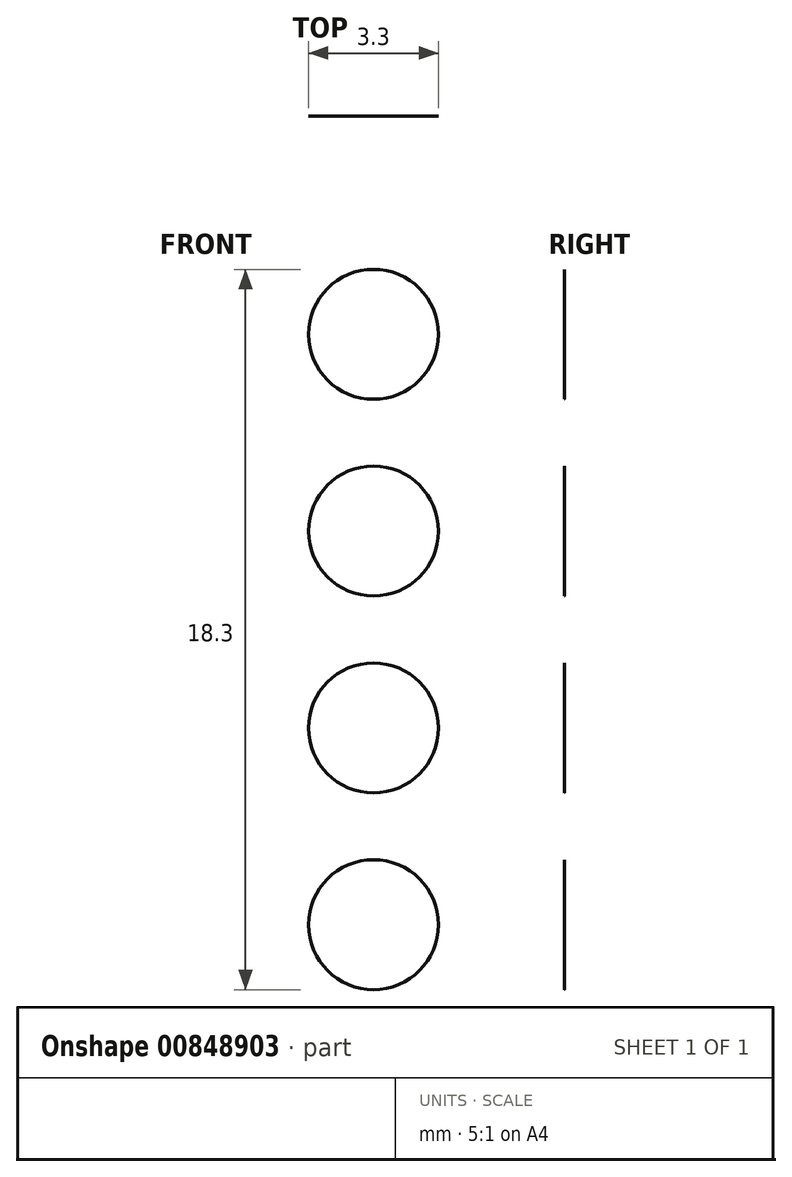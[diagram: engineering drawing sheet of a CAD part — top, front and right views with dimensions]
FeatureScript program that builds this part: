
annotation { "Feature Type Name" : "Feature", "Feature Type Description" : "" }
export const myFeature = defineFeature(function(context is Context, id is Id, definition is map)
    precondition{}
    {
        {
            var Q0;
            Q0=qCreatedBy(makeId("Front.planeOp"),FACE);
            var sketch = newSketch(context, id + "F0", { "sketchPlane" : qUnion([Q0])});
            skCircle(sketch, "E0", {"center": v(0, 0) * mm, "radius": 1.59 * mm});
            skLineSegment(sketch, "E1.direction1", {"start": v(0, 0) * mm, "end": v(25, 0) * mm, "construction": true});
            skLineSegment(sketch, "E2", {"start": v(0, 0) * mm, "end": v(0, 35.3) * mm, "construction": true});
            skCircle(sketch, "E3.0.1.0", {"center": v(0, 5) * mm, "radius": 1.59 * mm});
            skCircle(sketch, "E3.0.2.0", {"center": v(0, 10) * mm, "radius": 1.59 * mm});
            skCircle(sketch, "E3.0.3.0", {"center": v(0, 15) * mm, "radius": 1.59 * mm});
            skLineSegment(sketch, "E3.direction2", {"start": v(0, 0) * mm, "end": v(0, 5) * mm, "construction": true});
            skCircle(sketch, "E4", {"center": v(0, 20) * mm, "radius": 1.65 * mm});
            skLineSegment(sketch, "E5.direction2", {"start": v(0, 20) * mm, "end": v(0, 25) * mm, "construction": true});
            skCircle(sketch, "E6.0.1.0", {"center": v(0, 25) * mm, "radius": 1.65 * mm});
            skCircle(sketch, "E6.0.2.0", {"center": v(0, 30) * mm, "radius": 1.65 * mm});
            skCircle(sketch, "E6.0.3.0", {"center": v(0, 35) * mm, "radius": 1.65 * mm});
            skLineSegment(sketch, "E6.direction1", {"start": v(0, 20) * mm, "end": v(25, 20) * mm, "construction": true});
            skLineSegment(sketch, "E7", {"start": v(0, 0) * mm, "end": v(0, -5) * mm, "construction": true});
            skCircle(sketch, "E8", {"center": v(0, -5) * mm, "radius": 1.5 * mm});
            skCircle(sketch, "E9.0.1.0", {"center": v(0, -10) * mm, "radius": 1.5 * mm});
            skCircle(sketch, "E9.0.2.0", {"center": v(0, -15) * mm, "radius": 1.5 * mm});
            skCircle(sketch, "E9.0.3.0", {"center": v(0, -20) * mm, "radius": 1.5 * mm});
            skLineSegment(sketch, "E9.direction1", {"start": v(0, -5) * mm, "end": v(25, -5) * mm, "construction": true});
            skLineSegment(sketch, "E9.direction2", {"start": v(0, -5) * mm, "end": v(0, -10) * mm, "construction": true});
            skSolve(sketch);
        }
        {
            var Q0;
            Q0=makeQuery(id+"F0.imprint","IMPRINT",FACE,{"disambiguationData":[TD([[makeQuery(id+"F0.imprint","IMPRINT",EDGE,{"derivedFrom":sQuery(id+"F0.wireOp",EDGE,"E6.0.3.0")}),1.0]])]});
            var Q1;
            Q1=makeQuery(id+"F0.imprint","IMPRINT",FACE,{"disambiguationData":[TD([[makeQuery(id+"F0.imprint","IMPRINT",EDGE,{"derivedFrom":sQuery(id+"F0.wireOp",EDGE,"E6.0.2.0")}),1.0]])]});
            var Q2;
            Q2=makeQuery(id+"F0.imprint","IMPRINT",FACE,{"disambiguationData":[TD([[makeQuery(id+"F0.imprint","IMPRINT",EDGE,{"derivedFrom":sQuery(id+"F0.wireOp",EDGE,"E6.0.1.0")}),1.0]])]});
            var Q3;
            Q3=makeQuery(id+"F0.imprint","IMPRINT",FACE,{"disambiguationData":[TD([[makeQuery(id+"F0.imprint","IMPRINT",EDGE,{"derivedFrom":sQuery(id+"F0.wireOp",EDGE,"E4")}),1.0]])]});
            extrude(context, id + "F1", {"entities" : qUnion([Q0, Q1, Q2, Q3]), "depth" : 1 / 203.2 * mm, "offsetDistance" : 25 * mm});
        }
    });
